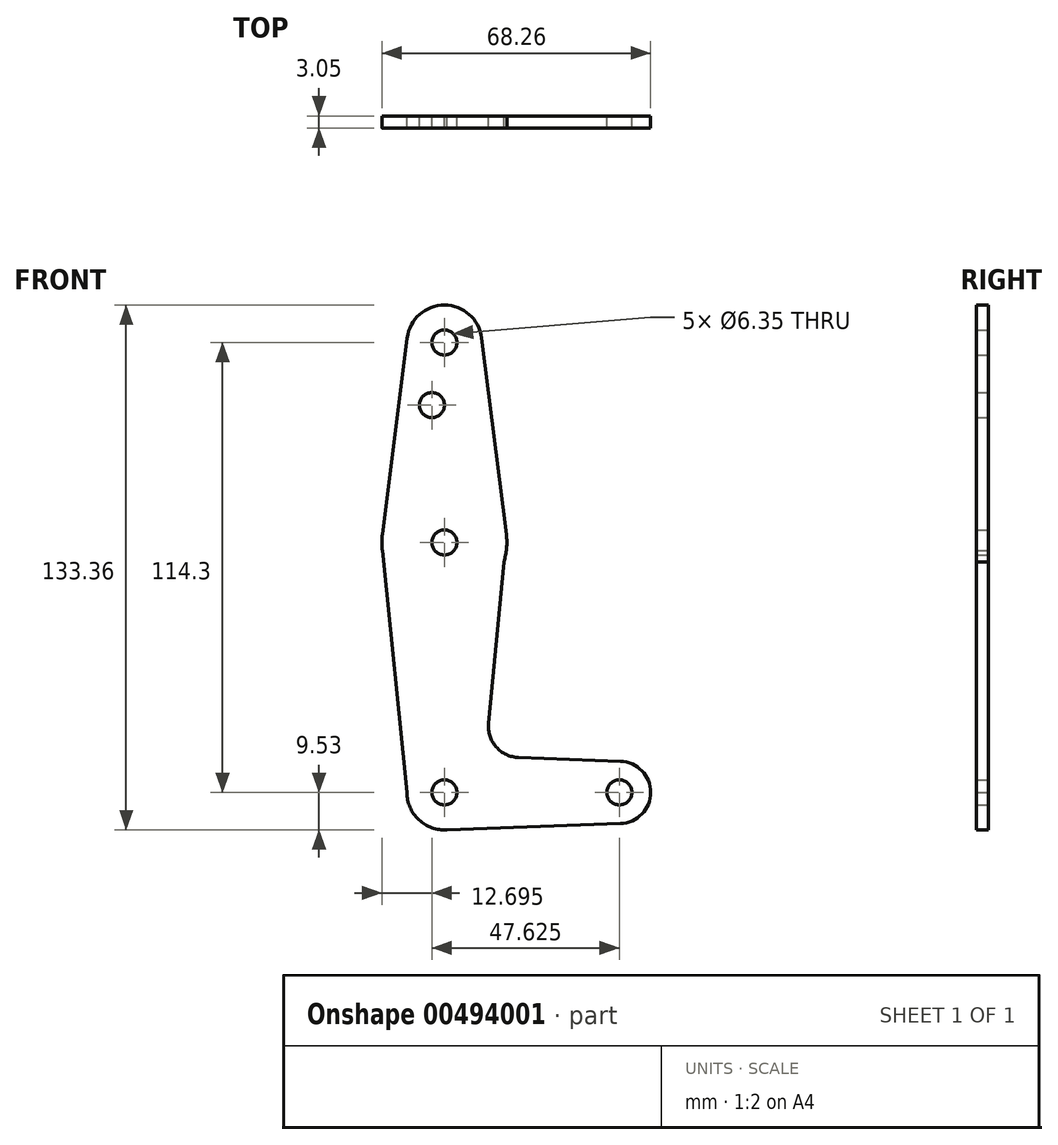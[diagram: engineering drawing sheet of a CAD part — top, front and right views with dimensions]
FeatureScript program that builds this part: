
annotation { "Feature Type Name" : "Feature", "Feature Type Description" : "" }
export const myFeature = defineFeature(function(context is Context, id is Id, definition is map)
    precondition{}
    {
        {
            var Q0;
            Q0=qCreatedBy(makeId("Front.planeOp"),FACE);
            var sketch = newSketch(context, id + "F0", { "sketchPlane" : qUnion([Q0])});
            skLineSegment(sketch, "E0", {"start": v(0, 0) * mm, "end": v(0, 114.3) * mm});
            skLineSegment(sketch, "E1", {"start": v(0, 0) * mm, "end": v(44.45, 0) * mm});
            skCircle(sketch, "E2", {"center": v(0, 114.3) * mm, "radius": 9.53 * mm});
            skCircle(sketch, "E3", {"center": v(0, 63.5) * mm, "radius": 15.88 * mm});
            skCircle(sketch, "E4", {"center": v(0, 0) * mm, "radius": 9.53 * mm});
            skCircle(sketch, "E5", {"center": v(44.45, 0) * mm, "radius": 7.94 * mm});
            skLineSegment(sketch, "E6", {"start": v(-9.45, 115.5) * mm, "end": v(-15.75, 65.48) * mm});
            skLineSegment(sketch, "E7", {"start": v(9.45, 115.5) * mm, "end": v(15.75, 65.48) * mm});
            skLineSegment(sketch, "E8", {"start": v(15.75, 65.48) * mm, "end": v(11.22, 17.55) * mm});
            skLineSegment(sketch, "E9", {"start": v(18.86, 8.85) * mm, "end": v(44.73, 7.93) * mm});
            skLineSegment(sketch, "E10", {"start": v(0, -9.53) * mm, "end": v(44.73, -7.93) * mm});
            skLineSegment(sketch, "E11", {"start": v(-15.75, 61.52) * mm, "end": v(-9.53, 0) * mm});
            skCircle(sketch, "E12", {"center": v(0, 63.5) * mm, "radius": 3.18 * mm});
            skCircle(sketch, "E13", {"center": v(0, 114.3) * mm, "radius": 3.18 * mm});
            skCircle(sketch, "E14", {"center": v(-3.18, 98.4) * mm, "radius": 3.18 * mm});
            skCircle(sketch, "E15", {"center": v(0, 0) * mm, "radius": 3.18 * mm});
            skCircle(sketch, "E16", {"center": v(44.45, 0) * mm, "radius": 3.18 * mm});
            skArc(sketch, "E17.filletArc", {"start": v(11.22, 17.55) * mm, "mid": v(13.16, 11.55) * mm, "end": v(18.86, 8.85) * mm});
            skSolve(sketch);
        }
        {
            var Q0;
            Q0 = qSketchRegion(id + "F0", true);
            var Q1;
            {var subQ0=sQuery(id+"F0.wireOp",EDGE,"E15");var subQ1=sQuery(id+"F0.wireOp",EDGE,"E0");var subQ2=makeQuery(id+"F0.imprint","INTERSECT",VERTEX,{"derivedFrom":[subQ1,subQ0]});Q1=makeQuery(id+"F0.imprint","IMPRINT",FACE,{"disambiguationData":[TD([[makeQuery(id+"F0.imprint","IMPRINT",EDGE,{"disambiguationData":[TD([[subQ2,-1.0]])],"derivedFrom":subQ1}),-1.0]])]});}
            extrude(context, id + "F1", {"entities" : qUnion([Q0, Q1]), "depth" : 3.05 * mm});
        }
    });
